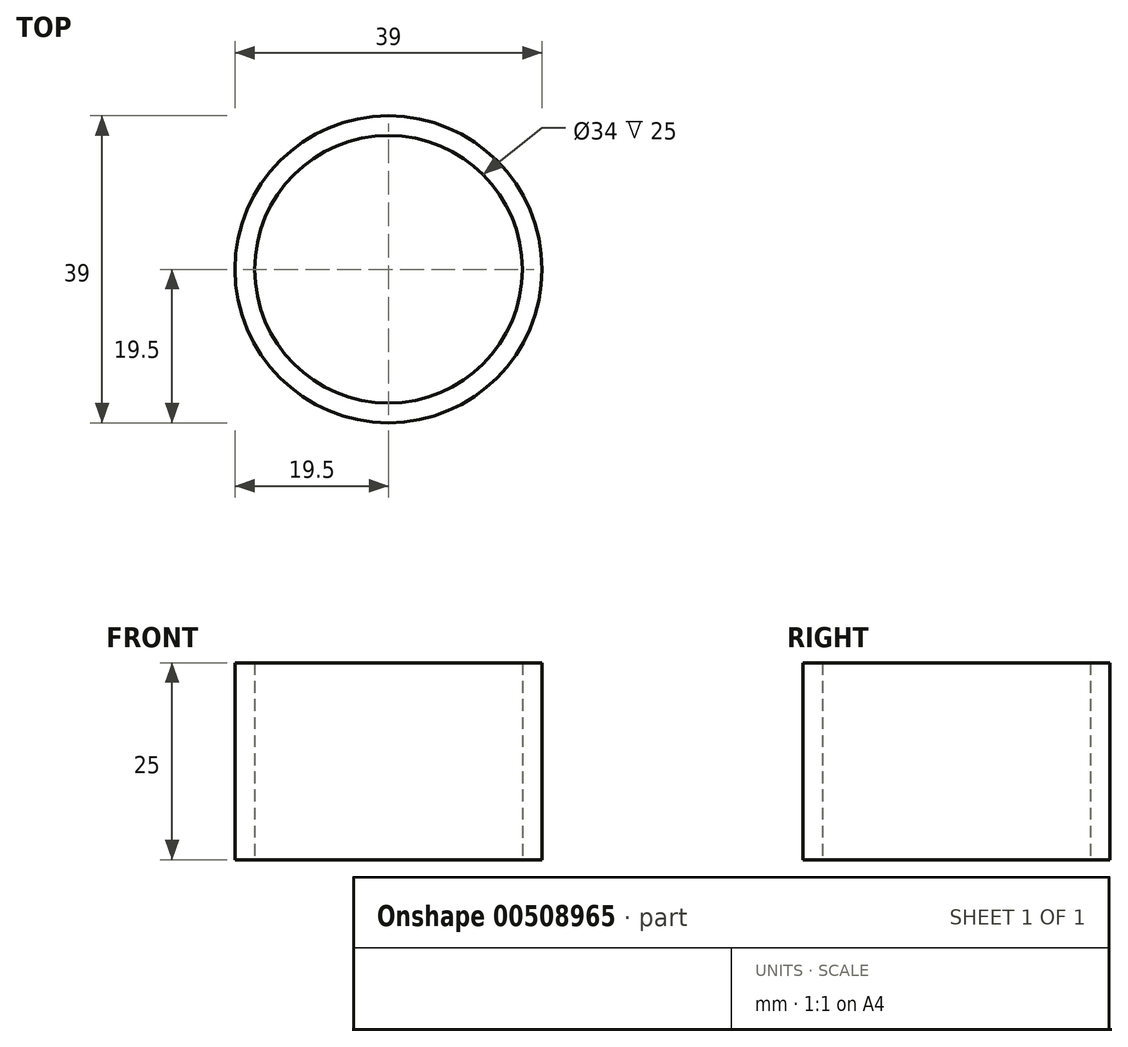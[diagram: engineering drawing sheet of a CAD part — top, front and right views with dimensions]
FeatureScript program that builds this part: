
annotation { "Feature Type Name" : "Feature", "Feature Type Description" : "" }
export const myFeature = defineFeature(function(context is Context, id is Id, definition is map)
    precondition{}
    {
        {
            var Q0;
            Q0=qCreatedBy(makeId("Top.planeOp"),FACE);
            var sketch = newSketch(context, id + "F0", { "sketchPlane" : qUnion([Q0])});
            skCircle(sketch, "E0", {"center": v(0, 0) * mm, "radius": 17 * mm});
            skCircle(sketch, "E1", {"center": v(0, 0) * mm, "radius": 19.5 * mm});
            skSolve(sketch);
        }
        {
            var Q0;
            Q0=makeQuery(id+"F0.imprint","IMPRINT",FACE,{"disambiguationData":[TD([[makeQuery(id+"F0.imprint","IMPRINT",EDGE,{"derivedFrom":sQuery(id+"F0.wireOp",EDGE,"E0")}),-1.0]])]});
            extrude(context, id + "F1", {"entities" : qUnion([Q0]), "depth" : 25 * mm, "offsetDistance" : 25 * mm});
        }
    });
